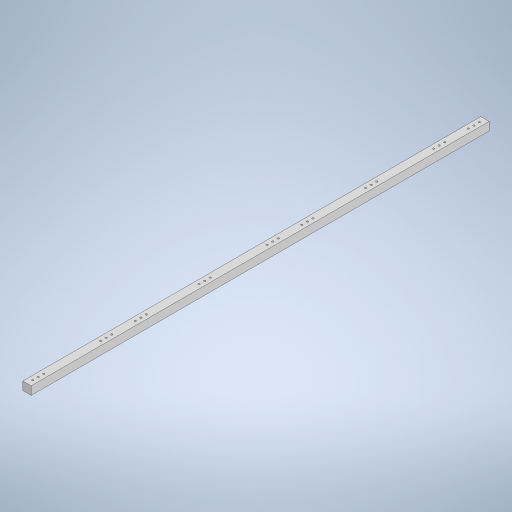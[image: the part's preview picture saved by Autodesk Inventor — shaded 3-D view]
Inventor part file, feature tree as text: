
AUTODESK INVENTOR PART (.ipt)
format: ipt  version: 2023 (Build 270158000, 158)  size: 285,184 bytes
history: native  units: mm
features: sketch x2, other x1, extrude x1, hole x1
ambient origin geometry x8: Origin, YZ Plane, XZ Plane, XY Plane, X Axis, Y Axis, Z Axis, Center Point
bodies: Body1 (feature_tree)
feature tree (5):
  other  "ソリッド1"
  extrude  "押し出し1"  Depth=15.0mm
  hole  "穴1"  [1 undecoded]
  sketch  "スケッチ1"
  sketch  "スケッチ2"
note: 1 required parameter value undecoded (feature->parameter linkage not recoverable at this tier; creation-order binding heuristic only, values carry confidence <= 0.55)
